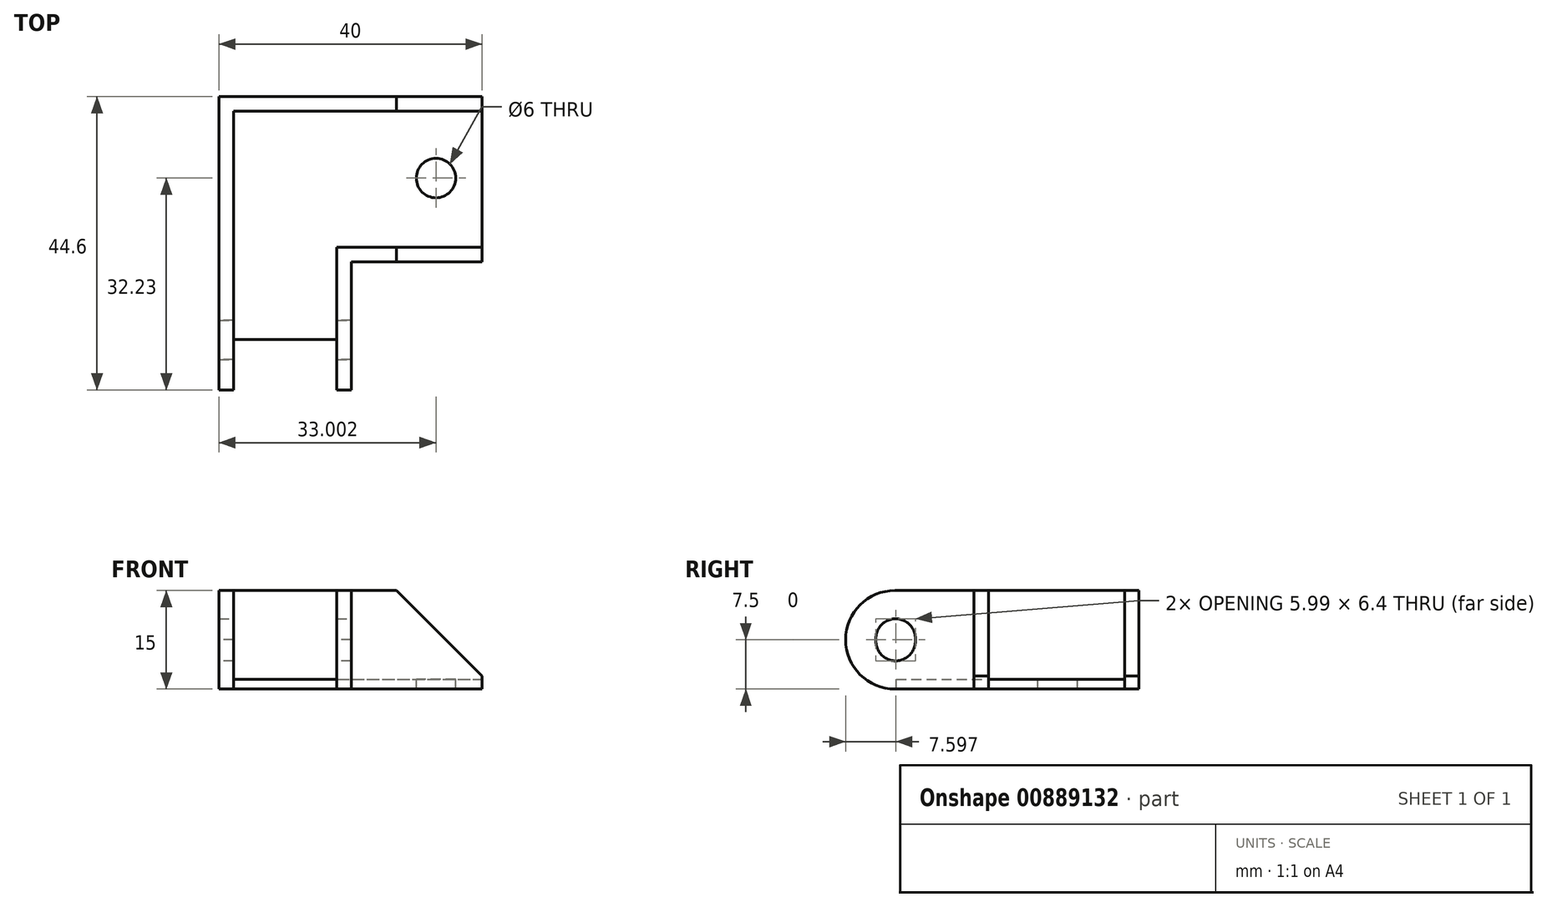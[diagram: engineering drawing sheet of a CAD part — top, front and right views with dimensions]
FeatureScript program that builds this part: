
annotation { "Feature Type Name" : "Feature", "Feature Type Description" : "" }
export const myFeature = defineFeature(function(context is Context, id is Id, definition is map)
    precondition{}
    {
        {
            var Q0;
            Q0=qCreatedBy(makeId("Top.planeOp"),FACE);
            var sketch = newSketch(context, id + "F0", { "sketchPlane" : qUnion([Q0])});
            skLineSegment(sketch, "E0.bottom", {"start": v(0, 0) * mm, "end": v(15.7, 0) * mm});
            skLineSegment(sketch, "E0.top", {"start": v(0, 19.5) * mm, "end": v(15.7, 19.5) * mm});
            skLineSegment(sketch, "E0.left", {"start": v(0, 0) * mm, "end": v(0, 19.5) * mm});
            skLineSegment(sketch, "E0.right", {"start": v(15.7, 0) * mm, "end": v(15.7, 19.5) * mm});
            skLineSegment(sketch, "E1.bottom", {"start": v(0, 19.5) * mm, "end": v(37.8, 19.5) * mm});
            skLineSegment(sketch, "E1.top", {"start": v(0, 40.2) * mm, "end": v(37.8, 40.2) * mm});
            skLineSegment(sketch, "E1.left", {"start": v(0, 19.5) * mm, "end": v(0, 40.2) * mm});
            skLineSegment(sketch, "E1.right", {"start": v(37.8, 19.5) * mm, "end": v(37.8, 40.2) * mm});
            skLineSegment(sketch, "E2.0", {"start": v(-2.2, -2.2) * mm, "end": v(-2.2, 19.5) * mm});
            skLineSegment(sketch, "E2.1", {"start": v(-2.2, -2.2) * mm, "end": v(17.9, -2.2) * mm});
            skLineSegment(sketch, "E2.2", {"start": v(17.9, -2.2) * mm, "end": v(17.9, 19.5) * mm});
            skLineSegment(sketch, "E3.0", {"start": v(-2.2, 42.4) * mm, "end": v(37.8, 42.4) * mm});
            skLineSegment(sketch, "E3.1", {"start": v(-2.2, 17.3) * mm, "end": v(-2.2, 42.4) * mm});
            skLineSegment(sketch, "E3.2", {"start": v(-2.2, 17.3) * mm, "end": v(37.8, 17.3) * mm});
            skLineSegment(sketch, "E4", {"start": v(37.8, 40.2) * mm, "end": v(37.8, 42.4) * mm});
            skLineSegment(sketch, "E5", {"start": v(37.8, 19.5) * mm, "end": v(37.8, 17.3) * mm});
            skLineSegment(sketch, "E6", {"start": v(0, 19.5) * mm, "end": v(0, 0) * mm});
            skLineSegment(sketch, "E7", {"start": v(0, 0) * mm, "end": v(0, -2.2) * mm});
            skLineSegment(sketch, "E8", {"start": v(15.7, 0) * mm, "end": v(15.7, -2.2) * mm});
            skSolve(sketch);
        }
        {
            var Q0;
            {var subQ4=sQuery(id+"F0.wireOp",EDGE,"E2.0");Q0=makeQuery(id+"F0.imprint","IMPRINT",FACE,{"disambiguationData":[TD([[makeQuery(id+"F0.imprint","IMPRINT",EDGE,{"derivedFrom":subQ4}),-1.0]])]});}
            var Q1;
            {var subQ7=sQuery(id+"F0.wireOp",EDGE,"E8");Q1=makeQuery(id+"F0.imprint","IMPRINT",FACE,{"disambiguationData":[TD([[makeQuery(id+"F0.imprint","IMPRINT",EDGE,{"derivedFrom":subQ7}),1.0]])]});}
            var Q2;
            {var subQ0=sQuery(id+"F0.wireOp",EDGE,"E5");Q2=makeQuery(id+"F0.imprint","IMPRINT",FACE,{"disambiguationData":[TD([[makeQuery(id+"F0.imprint","IMPRINT",EDGE,{"derivedFrom":subQ0}),-1.0]])]});}
            var Q3;
            {var subQ0=sQuery(id+"F0.wireOp",EDGE,"E1.bottom");var subQ1=sQuery(id+"F0.wireOp",EDGE,"E0.right");var subQ2=makeQuery(id+"F0.imprint","INTERSECT",VERTEX,{"derivedFrom":[subQ1,subQ0]});Q3=makeQuery(id+"F0.imprint","IMPRINT",FACE,{"disambiguationData":[TD([[makeQuery(id+"F0.imprint","IMPRINT",EDGE,{"disambiguationData":[TD([[subQ2,1.0]])],"derivedFrom":subQ1}),-1.0]])]});}
            var Q4;
            Q4=makeQuery(id+"F0.imprint","IMPRINT",FACE,{"disambiguationData":[TD([[makeQuery(id+"F0.imprint","IMPRINT",EDGE,{"derivedFrom":sQuery(id+"F0.wireOp",EDGE,"E1.top")}),1.0]])]});
            extrude(context, id + "F1", {"entities" : qUnion([Q0, Q1, Q2, Q3, Q4]), "depth" : 15 * mm, "offsetDistance" : 25 * mm});
        }
        {
            var Q0;
            Q0=makeQuery(id+"F0.imprint","IMPRINT",FACE,{"disambiguationData":[TD([[makeQuery(id+"F0.imprint","IMPRINT",EDGE,{"derivedFrom":sQuery(id+"F0.wireOp",EDGE,"E1.top")}),-1.0]])]});
            var Q1;
            {var subQ0=sQuery(id+"F0.wireOp",EDGE,"E0.bottom");Q1=makeQuery(id+"F0.imprint","IMPRINT",FACE,{"disambiguationData":[TD([[makeQuery(id+"F0.imprint","IMPRINT",EDGE,{"derivedFrom":subQ0}),1.0]])]});}
            var Q2;
            {var subQ0=sQuery(id+"F0.wireOp",EDGE,"E1.bottom");var subQ1=sQuery(id+"F0.wireOp",EDGE,"E0.right");var subQ2=makeQuery(id+"F0.imprint","INTERSECT",VERTEX,{"derivedFrom":[subQ1,subQ0]});Q2=makeQuery(id+"F0.imprint","IMPRINT",FACE,{"disambiguationData":[TD([[makeQuery(id+"F0.imprint","IMPRINT",EDGE,{"disambiguationData":[TD([[subQ2,1.0]])],"derivedFrom":subQ1}),1.0]])]});}
            extrude(context, id + "F2", {"entities" : qUnion([Q0, Q1, Q2]), "depth" : 1.5 * mm, "offsetDistance" : 25 * mm});
        }
        {
            var Q0;
            Q0=makeQuery(id+"F2.opExtrude","CAP_FACE",FACE,{"disambiguationData":[OSD([sQuery(id+"F0.wireOp",EDGE,"E0.bottom"),sQuery(id+"F0.wireOp",EDGE,"E0.right"),sQuery(id+"F0.wireOp",EDGE,"E1.bottom"),sQuery(id+"F0.wireOp",EDGE,"E1.top"),sQuery(id+"F0.wireOp",EDGE,"E1.left"),sQuery(id+"F0.wireOp",EDGE,"E1.right"),sQuery(id+"F0.wireOp",EDGE,"E6")])],"isStart":false});
            var sketch = newSketch(context, id + "F3", { "sketchPlane" : qUnion([Q0])});
            skCircle(sketch, "E9", {"center": v(30.8, 30.03) * mm, "radius": 3 * mm});
            skSolve(sketch);
        }
        {
            var Q0;
            Q0=makeQuery(id+"F3.imprint","IMPRINT",FACE,{"disambiguationData":[TD([[makeQuery(id+"F3.imprint","IMPRINT",EDGE,{"derivedFrom":sQuery(id+"F3.wireOp",EDGE,"E9")}),1.0]])]});
            extrude(context, id + "F4", {"entities" : qUnion([Q0]), "operationType" : NewBodyOperationType.REMOVE, "oppositeDirection" : true, "depth" : 25 * mm, "offsetDistance" : 25 * mm});
        }
        {
            var Q0;
            Q0=makeQuery(id+"F1.opExtrude","SWEPT_FACE",FACE,{"disambiguationData":[OSD([sQuery(id+"F0.wireOp",EDGE,"E2.2")])]});
            var sketch = newSketch(context, id + "F5", { "sketchPlane" : qUnion([Q0])});
            skCircle(sketch, "E10", {"center": v(5.4, 7.7) * mm, "radius": 3 * mm});
            skSolve(sketch);
        }
        {
            var Q0;
            Q0=makeQuery(id+"F5.imprint","IMPRINT",FACE,{"disambiguationData":[TD([[makeQuery(id+"F5.imprint","IMPRINT",EDGE,{"derivedFrom":sQuery(id+"F5.wireOp",EDGE,"E10")}),1.0]])]});
            extrude(context, id + "F6", {"entities" : qUnion([Q0]), "operationType" : NewBodyOperationType.REMOVE, "oppositeDirection" : true, "depth" : 25 * mm, "offsetDistance" : 25 * mm});
        }
        {
            var Q0;
            Q0=makeQuery(id+"F1.opExtrude","SWEPT_FACE",FACE,{"disambiguationData":[OSD([sQuery(id+"F0.wireOp",EDGE,"E2.0"),sQuery(id+"F0.wireOp",EDGE,"E3.1")])]});
            var sketch = newSketch(context, id + "F7", { "sketchPlane" : qUnion([Q0])});
            skCircle(sketch, "E11", {"center": v(-5.4, 7.3) * mm, "radius": 3 * mm});
            skSolve(sketch);
        }
        {
            var Q0;
            Q0=makeQuery(id+"F7.imprint","IMPRINT",FACE,{"disambiguationData":[TD([[makeQuery(id+"F7.imprint","IMPRINT",EDGE,{"derivedFrom":sQuery(id+"F7.wireOp",EDGE,"E11")}),1.0]])]});
            extrude(context, id + "F8", {"entities" : qUnion([Q0]), "operationType" : NewBodyOperationType.REMOVE, "oppositeDirection" : true, "depth" : 25 * mm, "offsetDistance" : 25 * mm});
        }
        {
            var Q0;
            {var subQ0=sQuery(id+"F0.wireOp",EDGE,"E2.1");Q0=makeQuery(id+"F1.opExtrude","CAP_EDGE",EDGE,{"disambiguationData":[OSD([subQ0]),TDD([makeQuery(id+"F0.imprint","IMPRINT",EDGE,{"disambiguationData":[TD([[makeQuery(id+"F0.imprint","INTERSECT",VERTEX,{"derivedFrom":[sQuery(id+"F0.wireOp",EDGE,"E2.0"),subQ0]}),-1.0]])],"derivedFrom":subQ0})])],"isStart":false});}
            var Q1;
            {var subQ0=sQuery(id+"F0.wireOp",EDGE,"E2.1");Q1=makeQuery(id+"F1.opExtrude","CAP_EDGE",EDGE,{"disambiguationData":[OSD([subQ0]),TDD([makeQuery(id+"F0.imprint","IMPRINT",EDGE,{"disambiguationData":[TD([[makeQuery(id+"F0.imprint","INTERSECT",VERTEX,{"derivedFrom":[subQ0,sQuery(id+"F0.wireOp",EDGE,"E2.2")]}),1.0]])],"derivedFrom":subQ0})])],"isStart":false});}
            var Q2;
            {var subQ0=sQuery(id+"F0.wireOp",EDGE,"E2.1");Q2=makeQuery(id+"F1.opExtrude","CAP_EDGE",EDGE,{"disambiguationData":[OSD([subQ0]),TDD([makeQuery(id+"F0.imprint","IMPRINT",EDGE,{"disambiguationData":[TD([[makeQuery(id+"F0.imprint","INTERSECT",VERTEX,{"derivedFrom":[sQuery(id+"F0.wireOp",EDGE,"E2.0"),subQ0]}),-1.0]])],"derivedFrom":subQ0})])],"isStart":true});}
            var Q3;
            {var subQ0=sQuery(id+"F0.wireOp",EDGE,"E2.1");Q3=makeQuery(id+"F1.opExtrude","CAP_EDGE",EDGE,{"disambiguationData":[OSD([subQ0]),TDD([makeQuery(id+"F0.imprint","IMPRINT",EDGE,{"disambiguationData":[TD([[makeQuery(id+"F0.imprint","INTERSECT",VERTEX,{"derivedFrom":[subQ0,sQuery(id+"F0.wireOp",EDGE,"E2.2")]}),1.0]])],"derivedFrom":subQ0})])],"isStart":true});}
            fillet(context, id + "F9", {"entities" : qUnion([Q0, Q1, Q2, Q3]), "radius" : 7.5 * mm, "tangentPropagation" : true, "allowEdgeOverflow" : false});
        }
        {
            var Q0;
            Q0=makeQuery(id+"F2.opExtrude","CAP_FACE",FACE,{"disambiguationData":[OSD([sQuery(id+"F0.wireOp",EDGE,"E0.bottom"),sQuery(id+"F0.wireOp",EDGE,"E0.right"),sQuery(id+"F0.wireOp",EDGE,"E1.bottom"),sQuery(id+"F0.wireOp",EDGE,"E1.top"),sQuery(id+"F0.wireOp",EDGE,"E1.left"),sQuery(id+"F0.wireOp",EDGE,"E1.right"),sQuery(id+"F0.wireOp",EDGE,"E6")])],"isStart":false});
            var sketch = newSketch(context, id + "F10", { "sketchPlane" : qUnion([Q0])});
            skLineSegment(sketch, "E12", {"start": v(15.7, 5.5) * mm, "end": v(0, 5.5) * mm});
            skSolve(sketch);
        }
        {
            var Q0;
            {var subQ0=sQuery(id+"F10.wireOp",EDGE,"E12");Q0=makeQuery(id+"F10.imprint","IMPRINT",FACE,{"disambiguationData":[TD([[makeQuery(id+"F10.imprint","IMPRINT",EDGE,{"derivedFrom":subQ0}),1.0]])]});}
            extrude(context, id + "F11", {"entities" : qUnion([Q0]), "operationType" : NewBodyOperationType.REMOVE, "oppositeDirection" : true, "depth" : 25 * mm, "offsetDistance" : 25 * mm});
        }
        {
            var Q0;
            Q0=makeQuery(id+"F1.opExtrude","CAP_EDGE",EDGE,{"disambiguationData":[OSD([sQuery(id+"F0.wireOp",EDGE,"E5")])],"isStart":false});
            var Q1;
            Q1=makeQuery(id+"F1.opExtrude","CAP_EDGE",EDGE,{"disambiguationData":[OSD([sQuery(id+"F0.wireOp",EDGE,"E4")])],"isStart":false});
            chamfer(context, id + "F12", {"entities" : qUnion([Q0, Q1]), "width" : 13 * mm, "tangentPropagation" : true});
        }
    });
